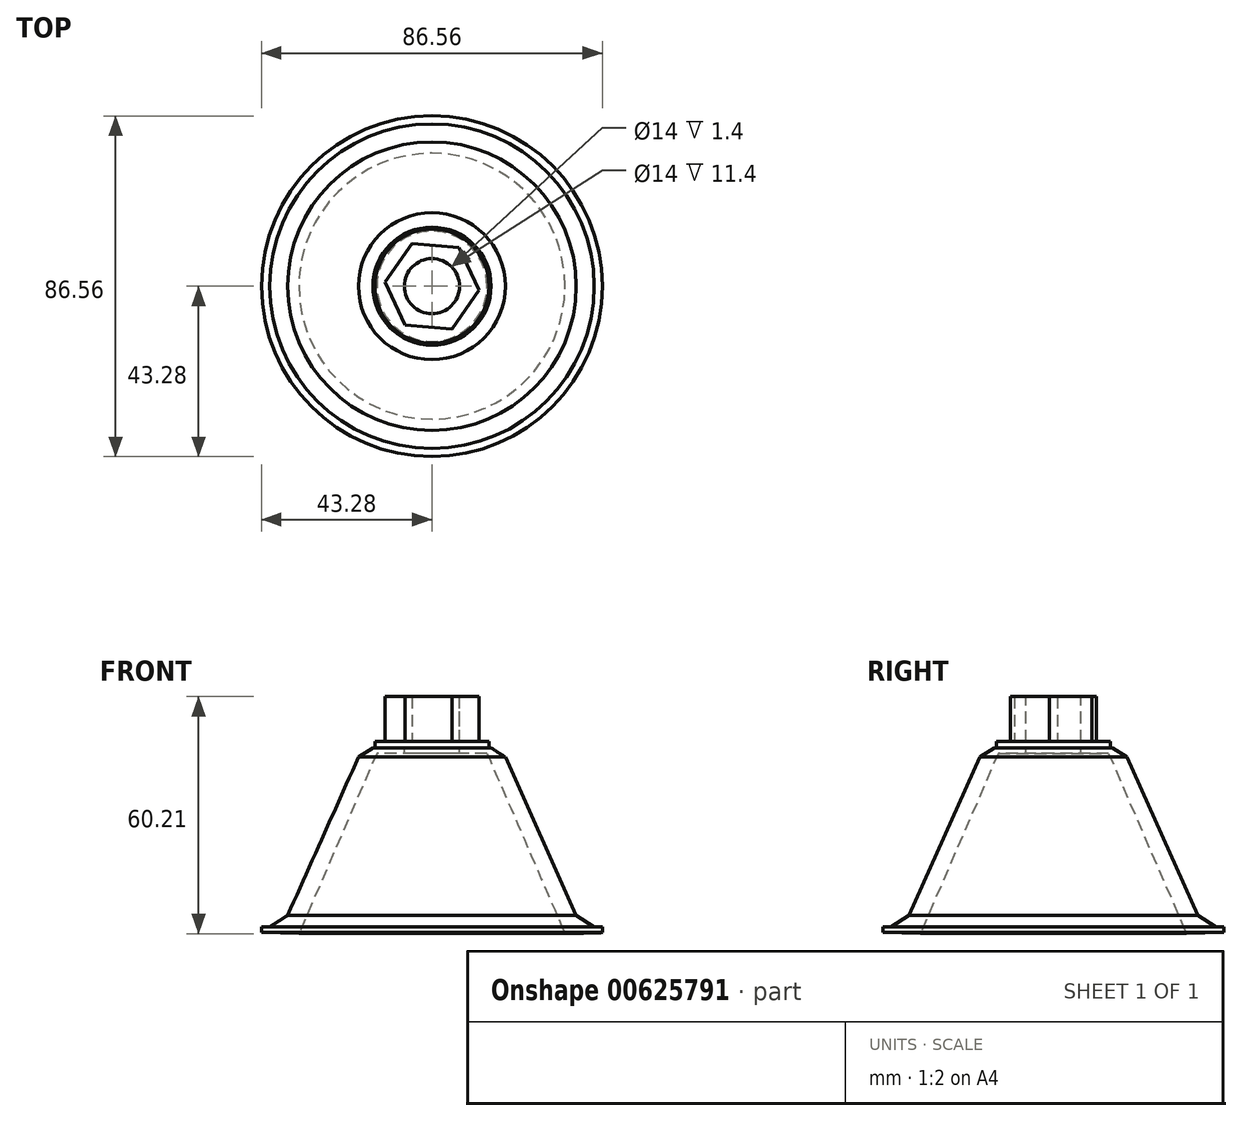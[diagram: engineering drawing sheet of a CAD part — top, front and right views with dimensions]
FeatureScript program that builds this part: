
annotation { "Feature Type Name" : "Feature", "Feature Type Description" : "" }
export const myFeature = defineFeature(function(context is Context, id is Id, definition is map)
    precondition{}
    {
        {
            var Q0;
            Q0=qCreatedBy(makeId("Front.planeOp"),FACE);
            var sketch = newSketch(context, id + "F0", { "sketchPlane" : qUnion([Q0])});
            skLineSegment(sketch, "E0", {"start": v(0, 24.4) * mm, "end": v(17.6, 24.4) * mm});
            skLineSegment(sketch, "E1", {"start": v(14, 23) * mm, "end": v(0, 23) * mm});
            skLineSegment(sketch, "E2", {"start": v(0, 24.4) * mm, "end": v(0, 23) * mm});
            skLineSegment(sketch, "E3", {"start": v(0, 0) * mm, "end": v(25.87, 3.89) * mm, "construction": true});
            skPoint(sketch, "E4.end.orphan", {"position": v(51.54, -9.87) * mm});
            skPoint(sketch, "E5.end.orphan", {"position": v(60.44, -9.87) * mm});
            skLineSegment(sketch, "E6", {"start": v(17.6, 24.4) * mm, "end": v(37.98, -21.15) * mm});
            skLineSegment(sketch, "E7", {"start": v(14, 23) * mm, "end": v(33.8, -22.8) * mm});
            skLineSegment(sketch, "E8", {"start": v(37.98, -21.15) * mm, "end": v(43.28, -21.15) * mm});
            skLineSegment(sketch, "E9", {"start": v(43.28, -21.15) * mm, "end": v(43.28, -22.55) * mm});
            skLineSegment(sketch, "E10", {"start": v(43.28, -22.55) * mm, "end": v(33.8, -22.8) * mm});
            skSolve(sketch);
        }
        {
            var Q0;
            Q0=qCreatedBy(makeId("Front.planeOp"),FACE);
            var sketch = newSketch(context, id + "F1", { "sketchPlane" : qUnion([Q0])});
            skLineSegment(sketch, "E11", {"start": v(0, 54.6) * mm, "end": v(0, -30.55) * mm, "construction": true});
            skSolve(sketch);
        }
        {
            var Q0;
            Q0 = qSketchRegion(id + "F1", true);
            var Q1;
            {var subQ1=sQuery(id+"F0.wireOp",EDGE,"E0");Q1=makeQuery(id+"F0.imprint","IMPRINT",FACE,{"disambiguationData":[TD([[makeQuery(id+"F0.imprint","IMPRINT",EDGE,{"derivedFrom":subQ1}),-1.0]])]});}
            var Q2;
            {var subQ4=sQuery(id+"F0.wireOp",EDGE,"VEq2pPUy-BK20-NXt4-UWRB-67ASPwkrfu8H");Q2=makeQuery(id+"F0.imprint","IMPRINT",FACE,{"disambiguationData":[TD([[makeQuery(id+"F0.imprint","IMPRINT",EDGE,{"derivedFrom":subQ4}),1.0]])]});}
            var Q3;
            Q3=sQuery(id+"F1.wireOp",EDGE,"E11");
            revolve(context, id + "F2", {"entities" : qUnion([Q0, Q1, Q2]), "axis" : qUnion([Q3]), "revolveType" : RevolveType.FULL});
        }
        {
            var Q0;
            Q0=makeQuery(id+"F2.opRevolve","SWEPT_FACE",FACE,{"disambiguationData":[OSD([sQuery(id+"F0.wireOp",EDGE,"E0")])]});
            var sketch = newSketch(context, id + "F3", { "sketchPlane" : qUnion([Q0])});
            skCircle(sketch, "E12.cCircle", {"center": v(0, 0) * mm, "radius": 12 * mm, "construction": true});
            skLineSegment(sketch, "E12.0", {"start": v(-6.86, -9.85) * mm, "end": v(-11.96, 1.02) * mm});
            skLineSegment(sketch, "E12.1", {"start": v(-11.96, 1.02) * mm, "end": v(-5.1, 10.86) * mm});
            skLineSegment(sketch, "E12.2", {"start": v(-5.1, 10.86) * mm, "end": v(6.86, 9.85) * mm});
            skLineSegment(sketch, "E12.3", {"start": v(6.86, 9.85) * mm, "end": v(11.96, -1.02) * mm});
            skLineSegment(sketch, "E12.4", {"start": v(11.96, -1.02) * mm, "end": v(5.1, -10.86) * mm});
            skLineSegment(sketch, "E12.5", {"start": v(5.1, -10.86) * mm, "end": v(-6.86, -9.85) * mm});
            skSolve(sketch);
        }
        {
            var Q0;
            Q0 = qSketchRegion(id + "F3", true);
            extrude(context, id + "F4", {"entities" : qUnion([Q0]), "operationType" : NewBodyOperationType.ADD, "depth" : 13 * mm, "offsetDistance" : 25 * mm});
        }
        {
            var Q0;
            Q0=makeQuery(id+"F4.opExtrude","CAP_FACE",FACE,{"disambiguationData":[OSD([sQuery(id+"F3.wireOp",EDGE,"E12.0"),sQuery(id+"F3.wireOp",EDGE,"E12.1"),sQuery(id+"F3.wireOp",EDGE,"E12.2"),sQuery(id+"F3.wireOp",EDGE,"E12.3"),sQuery(id+"F3.wireOp",EDGE,"E12.4"),sQuery(id+"F3.wireOp",EDGE,"E12.5")])],"isStart":false});
            var sketch = newSketch(context, id + "F5", { "sketchPlane" : qUnion([Q0])});
            skCircle(sketch, "E13", {"center": v(0, 0) * mm, "radius": 7 * mm});
            skSolve(sketch);
        }
        {
            var Q0;
            Q0 = qSketchRegion(id + "F5", true);
            extrude(context, id + "F6", {"entities" : qUnion([Q0]), "operationType" : NewBodyOperationType.REMOVE, "oppositeDirection" : true, "depth" : 15 * mm, "offsetDistance" : 25 * mm});
        }
        {
            var Q0;
            Q0=makeQuery(id+"F2.opRevolve","SWEPT_FACE",FACE,{"disambiguationData":[OSD([sQuery(id+"F0.wireOp",EDGE,"E0")])]});
            var sketch = newSketch(context, id + "F7", { "sketchPlane" : qUnion([Q0])});
            skCircle(sketch, "E14", {"center": v(0, 0) * mm, "radius": 14.5 * mm});
            skSolve(sketch);
        }
        {
            var Q0;
            Q0 = qSketchRegion(id + "F7", true);
            extrude(context, id + "F8", {"entities" : qUnion([Q0]), "operationType" : NewBodyOperationType.ADD, "depth" : 1.6 * mm, "offsetDistance" : 25 * mm});
        }
        {
            var Q0;
            Q0=makeQuery(id+"F2.opRevolve","SWEPT_EDGE",EDGE,{"disambiguationData":[OSD([sQuery(id+"F0.wireOp",EDGE,"E0"),sQuery(id+"F0.wireOp",EDGE,"E6")])]});
            chamfer(context, id + "F9", {"entities" : qUnion([Q0]), "width" : 4 * mm, "tangentPropagation" : true});
        }
        {
            var Q0;
            Q0=makeQuery(id+"F2.opRevolve","SWEPT_EDGE",EDGE,{"disambiguationData":[OSD([sQuery(id+"F0.wireOp",EDGE,"E6"),sQuery(id+"F0.wireOp",EDGE,"E8")])]});
            chamfer(context, id + "F10", {"entities" : qUnion([Q0]), "width" : 5 * mm, "tangentPropagation" : true});
        }
    });
